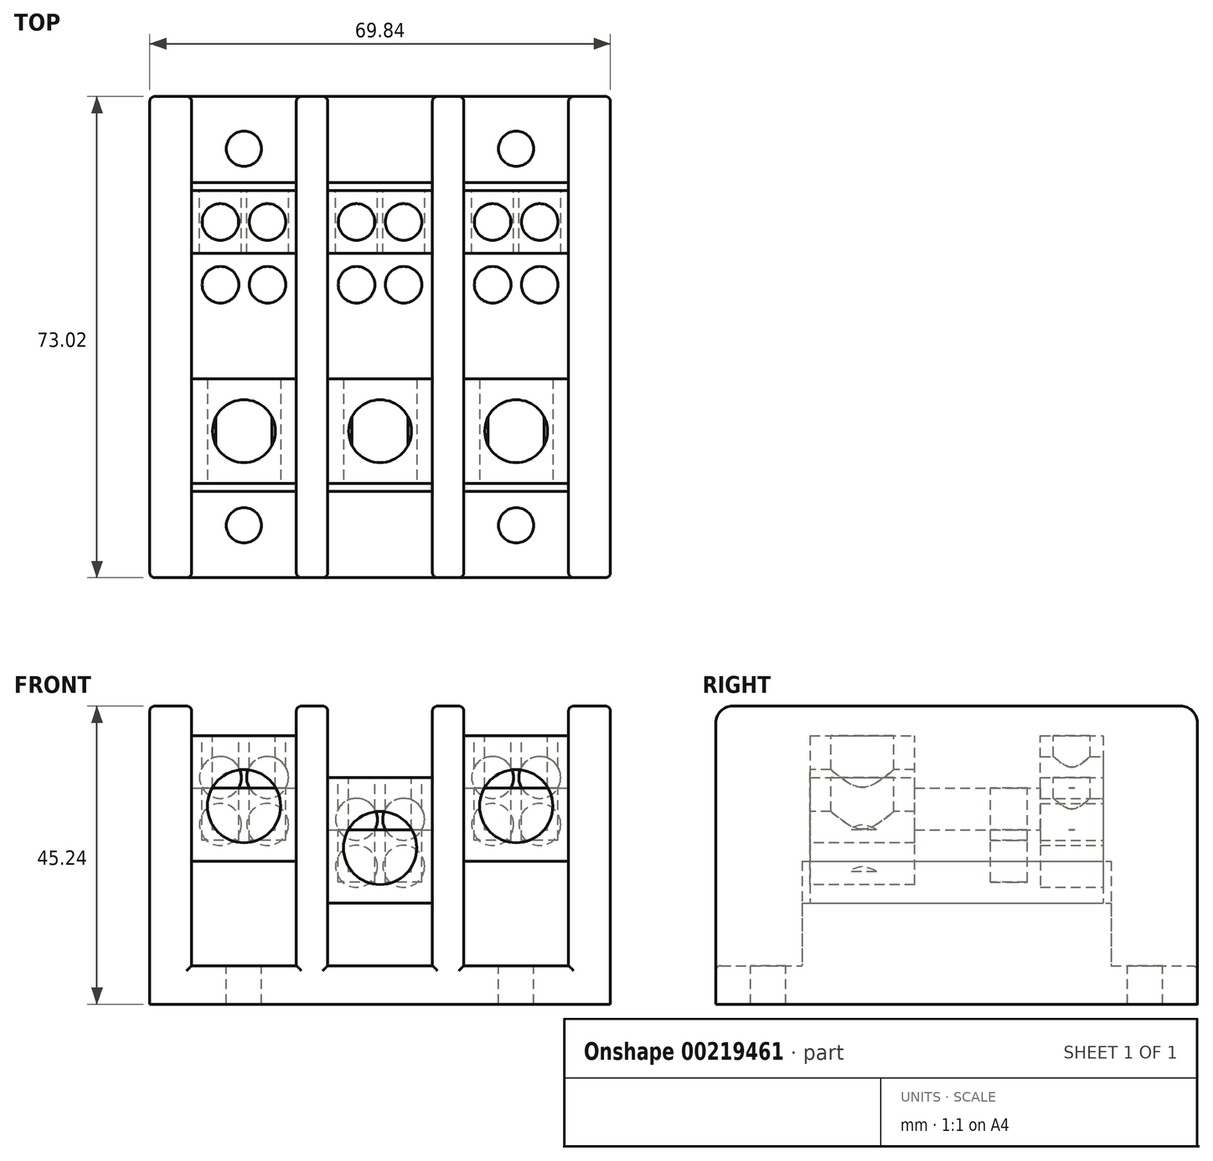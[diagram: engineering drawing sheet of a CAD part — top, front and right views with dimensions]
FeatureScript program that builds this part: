
annotation { "Feature Type Name" : "Feature", "Feature Type Description" : "" }
export const myFeature = defineFeature(function(context is Context, id is Id, definition is map)
    precondition{}
    {
        {
            var Q0;
            Q0=qCreatedBy(makeId("Top.planeOp"),FACE);
            var sketch = newSketch(context, id + "F0", { "sketchPlane" : qUnion([Q0])});
            skLineSegment(sketch, "E0.bottom", {"start": v(-34.92, -36.51) * mm, "end": v(34.93, -36.51) * mm});
            skLineSegment(sketch, "E0.top", {"start": v(-34.93, 36.51) * mm, "end": v(34.92, 36.51) * mm});
            skLineSegment(sketch, "E0.left", {"start": v(-34.92, -36.51) * mm, "end": v(-34.93, 36.51) * mm});
            skLineSegment(sketch, "E0.right", {"start": v(34.93, -36.51) * mm, "end": v(34.92, 36.51) * mm});
            skPoint(sketch, "E0.middle", {"position": v(0, 0) * mm});
            skSolve(sketch);
        }
        {
            var Q0;
            Q0=qSketchRegion(id+"F0",true);
            extrude(context, id + "F1", {"entities" : qUnion([Q0]), "depth" : 45.24 * mm});
        }
        {
            var Q0;
            Q0=makeQuery(id+"F1.opExtrude","CAP_FACE",FACE,{"disambiguationData":[OSD([sQuery(id+"F0.wireOp",EDGE,"E0.bottom"),sQuery(id+"F0.wireOp",EDGE,"E0.top"),sQuery(id+"F0.wireOp",EDGE,"E0.left"),sQuery(id+"F0.wireOp",EDGE,"E0.right")])],"isStart":false});
            var sketch = newSketch(context, id + "F2", { "sketchPlane" : qUnion([Q0])});
            skLineSegment(sketch, "E1.bottom", {"start": v(-12.7, -36.51) * mm, "end": v(-28.58, -36.51) * mm});
            skLineSegment(sketch, "E1.top", {"start": v(-12.7, 36.51) * mm, "end": v(-28.58, 36.51) * mm});
            skLineSegment(sketch, "E1.left", {"start": v(-12.7, -36.51) * mm, "end": v(-12.7, 36.51) * mm});
            skLineSegment(sketch, "E1.right", {"start": v(-28.58, -36.51) * mm, "end": v(-28.58, 36.51) * mm});
            skPoint(sketch, "E1.middle", {"position": v(-20.64, 0) * mm});
            skLineSegment(sketch, "E2.bottom", {"start": v(7.94, -36.51) * mm, "end": v(-7.94, -36.51) * mm});
            skLineSegment(sketch, "E2.top", {"start": v(7.94, 36.51) * mm, "end": v(-7.94, 36.51) * mm});
            skLineSegment(sketch, "E2.left", {"start": v(7.94, -36.51) * mm, "end": v(7.94, 36.51) * mm});
            skLineSegment(sketch, "E2.right", {"start": v(-7.94, -36.51) * mm, "end": v(-7.94, 36.51) * mm});
            skPoint(sketch, "E2.middle", {"position": v(0, 0) * mm});
            skLineSegment(sketch, "E3.bottom", {"start": v(28.58, -36.51) * mm, "end": v(12.7, -36.51) * mm});
            skLineSegment(sketch, "E3.top", {"start": v(28.58, 36.51) * mm, "end": v(12.7, 36.51) * mm});
            skLineSegment(sketch, "E3.left", {"start": v(28.58, -36.51) * mm, "end": v(28.58, 36.51) * mm});
            skLineSegment(sketch, "E3.right", {"start": v(12.7, -36.51) * mm, "end": v(12.7, 36.51) * mm});
            skPoint(sketch, "E3.middle", {"position": v(20.64, 0) * mm});
            skSolve(sketch);
        }
        {
            var Q0;
            Q0=qSketchRegion(id+"F2",true);
            extrude(context, id + "F3", {"entities" : qUnion([Q0]), "operationType" : NewBodyOperationType.REMOVE, "oppositeDirection" : true, "depth" : 39.4 * mm});
        }
        {
            var Q0;
            Q0=makeQuery(id+"F3.boolean.opBoolean","COPY",FACE,{"derivedFrom":makeQuery(id+"F3.opExtrude","CAP_FACE",FACE,{"disambiguationData":[OSD([sQuery(id+"F2.wireOp",EDGE,"E2.bottom"),sQuery(id+"F2.wireOp",EDGE,"E2.top"),sQuery(id+"F2.wireOp",EDGE,"E2.left"),sQuery(id+"F2.wireOp",EDGE,"E2.right")])],"isStart":false})});
            var sketch = newSketch(context, id + "F4", { "sketchPlane" : qUnion([Q0])});
            skCircle(sketch, "E4", {"center": v(-20.64, 28.57) * mm, "radius": 2.67 * mm});
            skCircle(sketch, "E5", {"center": v(-20.64, -28.58) * mm, "radius": 2.67 * mm});
            skCircle(sketch, "E6", {"center": v(20.64, 28.58) * mm, "radius": 2.67 * mm});
            skCircle(sketch, "E7", {"center": v(20.64, -28.57) * mm, "radius": 2.67 * mm});
            skSolve(sketch);
        }
        {
            var Q0;
            Q0=qSketchRegion(id+"F4",true);
            extrude(context, id + "F5", {"entities" : qUnion([Q0]), "operationType" : NewBodyOperationType.REMOVE, "oppositeDirection" : true, "depth" : 5.84 * mm});
        }
        {
            var Q0;
            {var subQ0=sQuery(id+"F0.wireOp",EDGE,"E0.left");var subQ1=sQuery(id+"F0.wireOp",EDGE,"E0.top");Q0=makeQuery(id+"F3.boolean.opBoolean","SPLIT",EDGE,{"disambiguationData":[TD([makeQuery(id+"F1.opExtrude","SWEPT_FACE",FACE,{"disambiguationData":[OSD([subQ0])]})])],"derivedFrom":makeQuery(id+"F1.opExtrude","CAP_EDGE",EDGE,{"disambiguationData":[OSD([subQ1])],"isStart":false})});}
            var Q1;
            {var subQ0=sQuery(id+"F0.wireOp",EDGE,"E0.top");Q1=makeQuery(id+"F3.boolean.opBoolean","SPLIT",EDGE,{"disambiguationData":[TD([makeQuery(id+"F3.opExtrude","SWEPT_FACE",FACE,{"disambiguationData":[OSD([sQuery(id+"F2.wireOp",EDGE,"E1.left")])]})])],"derivedFrom":makeQuery(id+"F1.opExtrude","CAP_EDGE",EDGE,{"disambiguationData":[OSD([subQ0])],"isStart":false})});}
            var Q2;
            {var subQ0=sQuery(id+"F0.wireOp",EDGE,"E0.top");Q2=makeQuery(id+"F3.boolean.opBoolean","SPLIT",EDGE,{"disambiguationData":[TD([makeQuery(id+"F3.opExtrude","SWEPT_FACE",FACE,{"disambiguationData":[OSD([sQuery(id+"F2.wireOp",EDGE,"E2.left")])]})])],"derivedFrom":makeQuery(id+"F1.opExtrude","CAP_EDGE",EDGE,{"disambiguationData":[OSD([subQ0])],"isStart":false})});}
            var Q3;
            {var subQ0=sQuery(id+"F0.wireOp",EDGE,"E0.right");var subQ1=sQuery(id+"F0.wireOp",EDGE,"E0.top");Q3=makeQuery(id+"F3.boolean.opBoolean","SPLIT",EDGE,{"disambiguationData":[TD([makeQuery(id+"F1.opExtrude","SWEPT_FACE",FACE,{"disambiguationData":[OSD([subQ0])]})])],"derivedFrom":makeQuery(id+"F1.opExtrude","CAP_EDGE",EDGE,{"disambiguationData":[OSD([subQ1])],"isStart":false})});}
            var Q4;
            {var subQ0=sQuery(id+"F0.wireOp",EDGE,"E0.bottom");var subQ1=sQuery(id+"F0.wireOp",EDGE,"E0.left");Q4=makeQuery(id+"F3.boolean.opBoolean","SPLIT",EDGE,{"disambiguationData":[TD([makeQuery(id+"F1.opExtrude","SWEPT_FACE",FACE,{"disambiguationData":[OSD([subQ1])]})])],"derivedFrom":makeQuery(id+"F1.opExtrude","CAP_EDGE",EDGE,{"disambiguationData":[OSD([subQ0])],"isStart":false})});}
            var Q5;
            {var subQ0=sQuery(id+"F0.wireOp",EDGE,"E0.bottom");Q5=makeQuery(id+"F3.boolean.opBoolean","SPLIT",EDGE,{"disambiguationData":[TD([makeQuery(id+"F3.opExtrude","SWEPT_FACE",FACE,{"disambiguationData":[OSD([sQuery(id+"F2.wireOp",EDGE,"E1.left")])]})])],"derivedFrom":makeQuery(id+"F1.opExtrude","CAP_EDGE",EDGE,{"disambiguationData":[OSD([subQ0])],"isStart":false})});}
            var Q6;
            {var subQ0=sQuery(id+"F0.wireOp",EDGE,"E0.bottom");Q6=makeQuery(id+"F3.boolean.opBoolean","SPLIT",EDGE,{"disambiguationData":[TD([makeQuery(id+"F3.opExtrude","SWEPT_FACE",FACE,{"disambiguationData":[OSD([sQuery(id+"F2.wireOp",EDGE,"E2.left")])]})])],"derivedFrom":makeQuery(id+"F1.opExtrude","CAP_EDGE",EDGE,{"disambiguationData":[OSD([subQ0])],"isStart":false})});}
            var Q7;
            {var subQ0=sQuery(id+"F0.wireOp",EDGE,"E0.bottom");var subQ1=sQuery(id+"F0.wireOp",EDGE,"E0.right");Q7=makeQuery(id+"F3.boolean.opBoolean","SPLIT",EDGE,{"disambiguationData":[TD([makeQuery(id+"F1.opExtrude","SWEPT_FACE",FACE,{"disambiguationData":[OSD([subQ1])]})])],"derivedFrom":makeQuery(id+"F1.opExtrude","CAP_EDGE",EDGE,{"disambiguationData":[OSD([subQ0])],"isStart":false})});}
            fillet(context, id + "F6", {"entities" : qUnion([Q0, Q1, Q2, Q3, Q4, Q5, Q6, Q7]), "radius" : 2.54 * mm, "tangentPropagation" : true});
        }
        {
            var Q0;
            Q0=makeQuery(id+"F1.opExtrude","SWEPT_EDGE",EDGE,{"disambiguationData":[OSD([sQuery(id+"F0.wireOp",EDGE,"E0.top"),sQuery(id+"F0.wireOp",EDGE,"E0.left")])]});
            var Q1;
            Q1=makeQuery(id+"F3.boolean.opBoolean","COPY",EDGE,{"derivedFrom":makeQuery(id+"F3.opExtrude","SWEPT_EDGE",EDGE,{"disambiguationData":[OSD([sQuery(id+"F0.wireOp",EDGE,"E0.top"),sQuery(id+"F2.wireOp",EDGE,"E1.top"),sQuery(id+"F2.wireOp",EDGE,"E1.right")])]})});
            var Q2;
            Q2=makeQuery(id+"F3.boolean.opBoolean","COPY",EDGE,{"derivedFrom":makeQuery(id+"F3.opExtrude","SWEPT_EDGE",EDGE,{"disambiguationData":[OSD([sQuery(id+"F0.wireOp",EDGE,"E0.top"),sQuery(id+"F2.wireOp",EDGE,"E1.top"),sQuery(id+"F2.wireOp",EDGE,"E1.left")])]})});
            var Q3;
            Q3=makeQuery(id+"F3.boolean.opBoolean","COPY",EDGE,{"derivedFrom":makeQuery(id+"F3.opExtrude","SWEPT_EDGE",EDGE,{"disambiguationData":[OSD([sQuery(id+"F0.wireOp",EDGE,"E0.top"),sQuery(id+"F2.wireOp",EDGE,"E2.top"),sQuery(id+"F2.wireOp",EDGE,"E2.right")])]})});
            var Q4;
            Q4=makeQuery(id+"F3.boolean.opBoolean","COPY",EDGE,{"derivedFrom":makeQuery(id+"F3.opExtrude","SWEPT_EDGE",EDGE,{"disambiguationData":[OSD([sQuery(id+"F0.wireOp",EDGE,"E0.top"),sQuery(id+"F2.wireOp",EDGE,"E2.top"),sQuery(id+"F2.wireOp",EDGE,"E2.left")])]})});
            var Q5;
            Q5=makeQuery(id+"F3.boolean.opBoolean","COPY",EDGE,{"derivedFrom":makeQuery(id+"F3.opExtrude","SWEPT_EDGE",EDGE,{"disambiguationData":[OSD([sQuery(id+"F0.wireOp",EDGE,"E0.top"),sQuery(id+"F2.wireOp",EDGE,"E3.top"),sQuery(id+"F2.wireOp",EDGE,"E3.right")])]})});
            var Q6;
            Q6=makeQuery(id+"F3.boolean.opBoolean","COPY",EDGE,{"derivedFrom":makeQuery(id+"F3.opExtrude","SWEPT_EDGE",EDGE,{"disambiguationData":[OSD([sQuery(id+"F0.wireOp",EDGE,"E0.top"),sQuery(id+"F2.wireOp",EDGE,"E3.top"),sQuery(id+"F2.wireOp",EDGE,"E3.left")])]})});
            var Q7;
            Q7=makeQuery(id+"F3.boolean.opBoolean","COPY",EDGE,{"derivedFrom":makeQuery(id+"F3.opExtrude","CAP_EDGE",EDGE,{"disambiguationData":[OSD([sQuery(id+"F2.wireOp",EDGE,"E3.top")])],"isStart":false})});
            var Q8;
            Q8=makeQuery(id+"F3.boolean.opBoolean","COPY",EDGE,{"derivedFrom":makeQuery(id+"F3.opExtrude","CAP_EDGE",EDGE,{"disambiguationData":[OSD([sQuery(id+"F2.wireOp",EDGE,"E2.top")])],"isStart":false})});
            var Q9;
            Q9=makeQuery(id+"F3.boolean.opBoolean","COPY",EDGE,{"derivedFrom":makeQuery(id+"F3.opExtrude","CAP_EDGE",EDGE,{"disambiguationData":[OSD([sQuery(id+"F2.wireOp",EDGE,"E1.top")])],"isStart":false})});
            var Q10;
            Q10=makeQuery(id+"F3.boolean.opBoolean","COPY",EDGE,{"derivedFrom":makeQuery(id+"F3.opExtrude","CAP_EDGE",EDGE,{"disambiguationData":[OSD([sQuery(id+"F2.wireOp",EDGE,"E1.bottom")])],"isStart":false})});
            var Q11;
            Q11=makeQuery(id+"F3.boolean.opBoolean","COPY",EDGE,{"derivedFrom":makeQuery(id+"F3.opExtrude","CAP_EDGE",EDGE,{"disambiguationData":[OSD([sQuery(id+"F2.wireOp",EDGE,"E2.bottom")])],"isStart":false})});
            var Q12;
            Q12=makeQuery(id+"F3.boolean.opBoolean","COPY",EDGE,{"derivedFrom":makeQuery(id+"F3.opExtrude","CAP_EDGE",EDGE,{"disambiguationData":[OSD([sQuery(id+"F2.wireOp",EDGE,"E3.bottom")])],"isStart":false})});
            var Q13;
            Q13=makeQuery(id+"F1.opExtrude","SWEPT_EDGE",EDGE,{"disambiguationData":[OSD([sQuery(id+"F0.wireOp",EDGE,"E0.bottom"),sQuery(id+"F0.wireOp",EDGE,"E0.right")])]});
            fillet(context, id + "F7", {"entities" : qUnion([Q0, Q1, Q2, Q3, Q4, Q5, Q6, Q7, Q8, Q9, Q10, Q11, Q12, Q13]), "radius" : 0.76 * mm, "tangentPropagation" : true});
        }
        {
            var Q0;
            Q0=makeQuery(id+"F3.boolean.opBoolean","COPY",FACE,{"derivedFrom":makeQuery(id+"F3.opExtrude","CAP_FACE",FACE,{"disambiguationData":[OSD([sQuery(id+"F2.wireOp",EDGE,"E1.bottom"),sQuery(id+"F2.wireOp",EDGE,"E1.top"),sQuery(id+"F2.wireOp",EDGE,"E1.left"),sQuery(id+"F2.wireOp",EDGE,"E1.right")])],"isStart":false})});
            var sketch = newSketch(context, id + "F8", { "sketchPlane" : qUnion([Q0])});
            skLineSegment(sketch, "E8.bottom", {"start": v(-28.58, 23.42) * mm, "end": v(-12.7, 23.42) * mm});
            skLineSegment(sketch, "E8.top", {"start": v(-28.58, -23.42) * mm, "end": v(-12.7, -23.42) * mm});
            skLineSegment(sketch, "E8.left", {"start": v(-28.58, 23.42) * mm, "end": v(-28.58, -23.42) * mm});
            skLineSegment(sketch, "E8.right", {"start": v(-12.7, 23.42) * mm, "end": v(-12.7, -23.42) * mm});
            skSolve(sketch);
        }
        {
            var Q0;
            Q0=qSketchRegion(id+"F8",true);
            extrude(context, id + "F9", {"entities" : qUnion([Q0]), "operationType" : NewBodyOperationType.ADD, "depth" : 15.88 * mm});
        }
        {
            var Q0;
            Q0=makeQuery(id+"F3.boolean.opBoolean","COPY",FACE,{"derivedFrom":makeQuery(id+"F3.opExtrude","CAP_FACE",FACE,{"disambiguationData":[OSD([sQuery(id+"F2.wireOp",EDGE,"E3.bottom"),sQuery(id+"F2.wireOp",EDGE,"E3.top"),sQuery(id+"F2.wireOp",EDGE,"E3.left"),sQuery(id+"F2.wireOp",EDGE,"E3.right")])],"isStart":false})});
            var sketch = newSketch(context, id + "F10", { "sketchPlane" : qUnion([Q0])});
            skLineSegment(sketch, "E9.bottom", {"start": v(12.7, 23.42) * mm, "end": v(28.58, 23.42) * mm});
            skLineSegment(sketch, "E9.top", {"start": v(12.7, -23.42) * mm, "end": v(28.58, -23.42) * mm});
            skLineSegment(sketch, "E9.left", {"start": v(12.7, 23.42) * mm, "end": v(12.7, -23.42) * mm});
            skLineSegment(sketch, "E9.right", {"start": v(28.58, 23.42) * mm, "end": v(28.58, -23.42) * mm});
            skSolve(sketch);
        }
        {
            var Q0;
            Q0=makeQuery(id+"F10.imprint","IMPRINT",FACE,{"disambiguationData":[TD([[makeQuery(id+"F10.imprint","IMPRINT",EDGE,{"derivedFrom":sQuery(id+"F10.wireOp",EDGE,"E9.bottom")}),-1.0]])]});
            extrude(context, id + "F11", {"entities" : qUnion([Q0]), "operationType" : NewBodyOperationType.ADD, "depth" : 15.88 * mm});
        }
        {
            var Q0;
            Q0=makeQuery(id+"F3.boolean.opBoolean","COPY",FACE,{"derivedFrom":makeQuery(id+"F3.opExtrude","CAP_FACE",FACE,{"disambiguationData":[OSD([sQuery(id+"F2.wireOp",EDGE,"E2.bottom"),sQuery(id+"F2.wireOp",EDGE,"E2.top"),sQuery(id+"F2.wireOp",EDGE,"E2.left"),sQuery(id+"F2.wireOp",EDGE,"E2.right")])],"isStart":false})});
            var sketch = newSketch(context, id + "F12", { "sketchPlane" : qUnion([Q0])});
            skLineSegment(sketch, "E10.bottom", {"start": v(-7.94, 23.42) * mm, "end": v(7.94, 23.42) * mm});
            skLineSegment(sketch, "E10.top", {"start": v(-7.94, -23.42) * mm, "end": v(7.94, -23.42) * mm});
            skLineSegment(sketch, "E10.left", {"start": v(-7.94, 23.42) * mm, "end": v(-7.94, -23.42) * mm});
            skLineSegment(sketch, "E10.right", {"start": v(7.94, 23.42) * mm, "end": v(7.94, -23.42) * mm});
            skSolve(sketch);
        }
        {
            var Q0;
            Q0=qSketchRegion(id+"F12",true);
            extrude(context, id + "F13", {"entities" : qUnion([Q0]), "operationType" : NewBodyOperationType.ADD, "depth" : 9.52 * mm});
        }
        {
            var Q0;
            Q0=makeQuery(id+"F9.opExtrude","CAP_FACE",FACE,{"disambiguationData":[OSD([sQuery(id+"F8.wireOp",EDGE,"E8.bottom"),sQuery(id+"F8.wireOp",EDGE,"E8.top"),sQuery(id+"F8.wireOp",EDGE,"E8.left"),sQuery(id+"F8.wireOp",EDGE,"E8.right")])],"isStart":false});
            var sketch = newSketch(context, id + "F14", { "sketchPlane" : qUnion([Q0])});
            skLineSegment(sketch, "E11.bottom", {"start": v(-28.57, -22.23) * mm, "end": v(-12.7, -22.23) * mm});
            skLineSegment(sketch, "E11.top", {"start": v(-28.58, 22.23) * mm, "end": v(-12.7, 22.23) * mm});
            skLineSegment(sketch, "E11.left", {"start": v(-28.57, -22.23) * mm, "end": v(-28.58, 22.23) * mm});
            skLineSegment(sketch, "E11.right", {"start": v(-12.7, -22.23) * mm, "end": v(-12.7, 22.23) * mm});
            skPoint(sketch, "E11.middle", {"position": v(-20.64, 0) * mm});
            skSolve(sketch);
        }
        {
            var Q0;
            Q0=qSketchRegion(id+"F14",true);
            extrude(context, id + "F15", {"entities" : qUnion([Q0]), "depth" : 19.05 * mm});
        }
        {
            var Q0;
            Q0=makeQuery(id+"F13.opExtrude","CAP_FACE",FACE,{"disambiguationData":[OSD([sQuery(id+"F12.wireOp",EDGE,"E10.bottom"),sQuery(id+"F12.wireOp",EDGE,"E10.top"),sQuery(id+"F12.wireOp",EDGE,"E10.left"),sQuery(id+"F12.wireOp",EDGE,"E10.right")])],"isStart":false});
            var sketch = newSketch(context, id + "F16", { "sketchPlane" : qUnion([Q0])});
            skLineSegment(sketch, "E12.bottom", {"start": v(-7.94, -22.22) * mm, "end": v(7.94, -22.22) * mm});
            skLineSegment(sketch, "E12.top", {"start": v(-7.94, 22.23) * mm, "end": v(7.94, 22.23) * mm});
            skLineSegment(sketch, "E12.left", {"start": v(-7.94, -22.22) * mm, "end": v(-7.94, 22.23) * mm});
            skLineSegment(sketch, "E12.right", {"start": v(7.94, -22.22) * mm, "end": v(7.94, 22.23) * mm});
            skPoint(sketch, "E12.middle", {"position": v(0, 0) * mm});
            skSolve(sketch);
        }
        {
            var Q0;
            Q0=makeQuery(id+"F16.imprint","IMPRINT",FACE,{"disambiguationData":[TD([[makeQuery(id+"F16.imprint","IMPRINT",EDGE,{"derivedFrom":sQuery(id+"F16.wireOp",EDGE,"E12.bottom")}),1.0]])]});
            extrude(context, id + "F17", {"entities" : qUnion([Q0]), "depth" : 19.05 * mm});
        }
        {
            var Q0;
            Q0=makeQuery(id+"F11.opExtrude","CAP_FACE",FACE,{"disambiguationData":[OSD([sQuery(id+"F10.wireOp",EDGE,"E9.bottom"),sQuery(id+"F10.wireOp",EDGE,"E9.top"),sQuery(id+"F10.wireOp",EDGE,"E9.left"),sQuery(id+"F10.wireOp",EDGE,"E9.right")])],"isStart":false});
            var sketch = newSketch(context, id + "F18", { "sketchPlane" : qUnion([Q0])});
            skLineSegment(sketch, "E13.bottom", {"start": v(12.7, -22.23) * mm, "end": v(28.58, -22.23) * mm});
            skLineSegment(sketch, "E13.top", {"start": v(12.7, 22.23) * mm, "end": v(28.58, 22.23) * mm});
            skLineSegment(sketch, "E13.left", {"start": v(12.7, -22.23) * mm, "end": v(12.7, 22.22) * mm});
            skLineSegment(sketch, "E13.right", {"start": v(28.58, -22.23) * mm, "end": v(28.58, 22.22) * mm});
            skPoint(sketch, "E13.middle", {"position": v(20.64, 0) * mm});
            skSolve(sketch);
        }
        {
            var Q0;
            Q0=qSketchRegion(id+"F18",true);
            extrude(context, id + "F19", {"entities" : qUnion([Q0]), "depth" : 19.05 * mm});
        }
        {
            var Q0;
            Q0=makeQuery(id+"F15.opExtrude","CAP_FACE",FACE,{"disambiguationData":[OSD([sQuery(id+"F14.wireOp",EDGE,"E11.bottom"),sQuery(id+"F14.wireOp",EDGE,"E11.top"),sQuery(id+"F14.wireOp",EDGE,"E11.left"),sQuery(id+"F14.wireOp",EDGE,"E11.right")])],"isStart":false});
            var sketch = newSketch(context, id + "F20", { "sketchPlane" : qUnion([Q0])});
            skLineSegment(sketch, "E14.bottom", {"start": v(-28.58, 12.7) * mm, "end": v(-12.7, 12.7) * mm});
            skLineSegment(sketch, "E14.top", {"start": v(-28.58, -6.35) * mm, "end": v(-12.7, -6.35) * mm});
            skLineSegment(sketch, "E14.left", {"start": v(-28.58, 12.7) * mm, "end": v(-28.58, -6.35) * mm});
            skLineSegment(sketch, "E14.right", {"start": v(-12.7, 12.7) * mm, "end": v(-12.7, -6.35) * mm});
            skSolve(sketch);
        }
        {
            var Q0;
            Q0=qSketchRegion(id+"F20",true);
            extrude(context, id + "F21", {"entities" : qUnion([Q0]), "operationType" : NewBodyOperationType.REMOVE, "oppositeDirection" : true, "depth" : 7.94 * mm});
        }
        {
            var Q0;
            {var subQ0=sQuery(id+"F14.wireOp",EDGE,"E11.top");var subQ1=sQuery(id+"F14.wireOp",EDGE,"E11.right");var subQ2=sQuery(id+"F14.wireOp",EDGE,"E11.left");Q0=makeQuery(id+"F21.boolean.opBoolean","SPLIT",FACE,{"disambiguationData":[TD([makeQuery(id+"F15.opExtrude","SWEPT_FACE",FACE,{"disambiguationData":[OSD([subQ0])]})])],"derivedFrom":makeQuery(id+"F15.opExtrude","CAP_FACE",FACE,{"disambiguationData":[OSD([sQuery(id+"F14.wireOp",EDGE,"E11.bottom"),subQ0,subQ2,subQ1])],"isStart":false})});}
            var sketch = newSketch(context, id + "F22", { "sketchPlane" : qUnion([Q0])});
            skCircle(sketch, "E15", {"center": v(-24.2, 17.46) * mm, "radius": 2.78 * mm});
            skCircle(sketch, "E16", {"center": v(-17.07, 17.46) * mm, "radius": 2.78 * mm});
            skPoint(sketch, "E17.centerSnap0", {"position": v(-20.64, -22.23) * mm});
            skSolve(sketch);
        }
        {
            var Q0;
            Q0=qSketchRegion(id+"F22",true);
            extrude(context, id + "F23", {"entities" : qUnion([Q0]), "operationType" : NewBodyOperationType.REMOVE, "oppositeDirection" : true, "depth" : 7.94 * mm});
        }
        {
            var Q0;
            {var subQ0=sQuery(id+"F14.wireOp",EDGE,"E11.bottom");var subQ1=sQuery(id+"F14.wireOp",EDGE,"E11.left");var subQ2=sQuery(id+"F14.wireOp",EDGE,"E11.right");Q0=makeQuery(id+"F21.boolean.opBoolean","SPLIT",FACE,{"disambiguationData":[TD([makeQuery(id+"F15.opExtrude","SWEPT_FACE",FACE,{"disambiguationData":[OSD([subQ0])]})])],"derivedFrom":makeQuery(id+"F15.opExtrude","CAP_FACE",FACE,{"disambiguationData":[OSD([subQ0,sQuery(id+"F14.wireOp",EDGE,"E11.top"),subQ1,subQ2])],"isStart":false})});}
            var sketch = newSketch(context, id + "F24", { "sketchPlane" : qUnion([Q0])});
            skCircle(sketch, "E18", {"center": v(-20.64, -14.29) * mm, "radius": 4.76 * mm});
            skPoint(sketch, "E18.centerSnap0", {"position": v(-28.58, -14.29) * mm});
            skPoint(sketch, "E18.centerSnap1", {"position": v(-20.64, -22.23) * mm});
            skSolve(sketch);
        }
        {
            var Q0;
            Q0=qSketchRegion(id+"F24",true);
            extrude(context, id + "F25", {"entities" : qUnion([Q0]), "operationType" : NewBodyOperationType.REMOVE, "oppositeDirection" : true, "depth" : 14.29 * mm});
        }
        {
            var Q0;
            Q0=makeQuery(id+"F21.boolean.opBoolean","COPY",FACE,{"derivedFrom":makeQuery(id+"F21.opExtrude","CAP_FACE",FACE,{"disambiguationData":[OSD([sQuery(id+"F20.wireOp",EDGE,"E14.bottom"),sQuery(id+"F20.wireOp",EDGE,"E14.top"),sQuery(id+"F20.wireOp",EDGE,"E14.left"),sQuery(id+"F20.wireOp",EDGE,"E14.right")])],"isStart":false})});
            var sketch = newSketch(context, id + "F26", { "sketchPlane" : qUnion([Q0])});
            skCircle(sketch, "E19", {"center": v(-24.2, 7.94) * mm, "radius": 2.78 * mm});
            skCircle(sketch, "E20", {"center": v(-17.07, 7.94) * mm, "radius": 2.78 * mm});
            skSolve(sketch);
        }
        {
            var Q0;
            Q0=qSketchRegion(id+"F26",true);
            extrude(context, id + "F27", {"entities" : qUnion([Q0]), "operationType" : NewBodyOperationType.REMOVE, "oppositeDirection" : true, "depth" : 7.94 * mm});
        }
        {
            var Q0;
            Q0=makeQuery(id+"F17.opExtrude","CAP_FACE",FACE,{"disambiguationData":[OSD([sQuery(id+"F16.wireOp",EDGE,"E12.bottom"),sQuery(id+"F16.wireOp",EDGE,"E12.top"),sQuery(id+"F16.wireOp",EDGE,"E12.left"),sQuery(id+"F16.wireOp",EDGE,"E12.right")])],"isStart":false});
            var sketch = newSketch(context, id + "F28", { "sketchPlane" : qUnion([Q0])});
            skLineSegment(sketch, "E21.bottom", {"start": v(-7.94, 12.7) * mm, "end": v(7.94, 12.7) * mm});
            skLineSegment(sketch, "E21.top", {"start": v(-7.94, -6.35) * mm, "end": v(7.94, -6.35) * mm});
            skLineSegment(sketch, "E21.left", {"start": v(-7.94, 12.7) * mm, "end": v(-7.94, -6.35) * mm});
            skLineSegment(sketch, "E21.right", {"start": v(7.94, 12.7) * mm, "end": v(7.94, -6.35) * mm});
            skSolve(sketch);
        }
        {
            var Q0;
            Q0=makeQuery(id+"F28.imprint","IMPRINT",FACE,{"disambiguationData":[TD([[makeQuery(id+"F28.imprint","IMPRINT",EDGE,{"derivedFrom":sQuery(id+"F28.wireOp",EDGE,"E21.bottom")}),-1.0]])]});
            extrude(context, id + "F29", {"entities" : qUnion([Q0]), "operationType" : NewBodyOperationType.REMOVE, "oppositeDirection" : true, "depth" : 7.94 * mm});
        }
        {
            var Q0;
            Q0=makeQuery(id+"F19.opExtrude","CAP_FACE",FACE,{"disambiguationData":[OSD([sQuery(id+"F18.wireOp",EDGE,"E13.bottom"),sQuery(id+"F18.wireOp",EDGE,"E13.top"),sQuery(id+"F18.wireOp",EDGE,"E13.left"),sQuery(id+"F18.wireOp",EDGE,"E13.right")])],"isStart":false});
            var sketch = newSketch(context, id + "F30", { "sketchPlane" : qUnion([Q0])});
            skLineSegment(sketch, "E22.bottom", {"start": v(12.7, 12.7) * mm, "end": v(28.58, 12.7) * mm});
            skLineSegment(sketch, "E22.top", {"start": v(12.7, -6.35) * mm, "end": v(28.58, -6.35) * mm});
            skLineSegment(sketch, "E22.left", {"start": v(12.7, 12.7) * mm, "end": v(12.7, -6.35) * mm});
            skLineSegment(sketch, "E22.right", {"start": v(28.58, 12.7) * mm, "end": v(28.58, -6.35) * mm});
            skSolve(sketch);
        }
        {
            var Q0;
            Q0=qSketchRegion(id+"F30",true);
            extrude(context, id + "F31", {"entities" : qUnion([Q0]), "operationType" : NewBodyOperationType.REMOVE, "oppositeDirection" : true, "depth" : 7.94 * mm});
        }
        {
            var Q0;
            {var subQ0=sQuery(id+"F16.wireOp",EDGE,"E12.top");var subQ1=sQuery(id+"F16.wireOp",EDGE,"E12.right");var subQ2=sQuery(id+"F16.wireOp",EDGE,"E12.left");Q0=makeQuery(id+"F29.boolean.opBoolean","SPLIT",FACE,{"disambiguationData":[TD([makeQuery(id+"F17.opExtrude","SWEPT_FACE",FACE,{"disambiguationData":[OSD([subQ0])]})])],"derivedFrom":makeQuery(id+"F17.opExtrude","CAP_FACE",FACE,{"disambiguationData":[OSD([sQuery(id+"F16.wireOp",EDGE,"E12.bottom"),subQ0,subQ2,subQ1])],"isStart":false})});}
            var sketch = newSketch(context, id + "F32", { "sketchPlane" : qUnion([Q0])});
            skCircle(sketch, "E23", {"center": v(-3.57, 17.46) * mm, "radius": 2.78 * mm});
            skPoint(sketch, "E23.centerSnap0", {"position": v(-7.94, 17.46) * mm});
            skCircle(sketch, "E24", {"center": v(3.57, 17.46) * mm, "radius": 2.78 * mm});
            skSolve(sketch);
        }
        {
            var Q0;
            Q0=qSketchRegion(id+"F32",true);
            extrude(context, id + "F33", {"entities" : qUnion([Q0]), "operationType" : NewBodyOperationType.REMOVE, "oppositeDirection" : true, "depth" : 7.94 * mm});
        }
        {
            var Q0;
            Q0=makeQuery(id+"F29.boolean.opBoolean","COPY",FACE,{"derivedFrom":makeQuery(id+"F29.opExtrude","CAP_FACE",FACE,{"disambiguationData":[OSD([sQuery(id+"F28.wireOp",EDGE,"E21.bottom"),sQuery(id+"F28.wireOp",EDGE,"E21.top"),sQuery(id+"F28.wireOp",EDGE,"E21.left"),sQuery(id+"F28.wireOp",EDGE,"E21.right")])],"isStart":false})});
            var sketch = newSketch(context, id + "F34", { "sketchPlane" : qUnion([Q0])});
            skCircle(sketch, "E25", {"center": v(-3.57, 7.94) * mm, "radius": 2.78 * mm});
            skCircle(sketch, "E26", {"center": v(3.57, 7.94) * mm, "radius": 2.78 * mm});
            skSolve(sketch);
        }
        {
            var Q0;
            Q0=qSketchRegion(id+"F34",true);
            extrude(context, id + "F35", {"entities" : qUnion([Q0]), "operationType" : NewBodyOperationType.REMOVE, "oppositeDirection" : true, "depth" : 7.94 * mm});
        }
        {
            var Q0;
            {var subQ0=sQuery(id+"F18.wireOp",EDGE,"E13.top");var subQ1=sQuery(id+"F18.wireOp",EDGE,"E13.right");var subQ2=sQuery(id+"F18.wireOp",EDGE,"E13.left");Q0=makeQuery(id+"F31.boolean.opBoolean","SPLIT",FACE,{"disambiguationData":[TD([makeQuery(id+"F19.opExtrude","SWEPT_FACE",FACE,{"disambiguationData":[OSD([subQ0])]})])],"derivedFrom":makeQuery(id+"F19.opExtrude","CAP_FACE",FACE,{"disambiguationData":[OSD([sQuery(id+"F18.wireOp",EDGE,"E13.bottom"),subQ0,subQ2,subQ1])],"isStart":false})});}
            var sketch = newSketch(context, id + "F36", { "sketchPlane" : qUnion([Q0])});
            skCircle(sketch, "E27", {"center": v(17.07, 17.46) * mm, "radius": 2.78 * mm});
            skPoint(sketch, "E27.centerSnap0", {"position": v(12.7, 17.46) * mm});
            skCircle(sketch, "E28", {"center": v(24.2, 17.46) * mm, "radius": 2.78 * mm});
            skPoint(sketch, "E28.centerSnap0", {"position": v(28.58, 17.46) * mm});
            skSolve(sketch);
        }
        {
            var Q0;
            Q0=qSketchRegion(id+"F36",true);
            extrude(context, id + "F37", {"entities" : qUnion([Q0]), "operationType" : NewBodyOperationType.REMOVE, "oppositeDirection" : true, "depth" : 7.94 * mm});
        }
        {
            var Q0;
            Q0=makeQuery(id+"F31.boolean.opBoolean","COPY",FACE,{"derivedFrom":makeQuery(id+"F31.opExtrude","CAP_FACE",FACE,{"disambiguationData":[OSD([sQuery(id+"F30.wireOp",EDGE,"E22.bottom"),sQuery(id+"F30.wireOp",EDGE,"E22.top"),sQuery(id+"F30.wireOp",EDGE,"E22.left"),sQuery(id+"F30.wireOp",EDGE,"E22.right")])],"isStart":false})});
            var sketch = newSketch(context, id + "F38", { "sketchPlane" : qUnion([Q0])});
            skCircle(sketch, "E29", {"center": v(17.07, 7.94) * mm, "radius": 2.78 * mm});
            skCircle(sketch, "E30", {"center": v(24.2, 7.94) * mm, "radius": 2.78 * mm});
            skSolve(sketch);
        }
        {
            var Q0;
            Q0=qSketchRegion(id+"F38",true);
            extrude(context, id + "F39", {"entities" : qUnion([Q0]), "operationType" : NewBodyOperationType.REMOVE, "oppositeDirection" : true, "depth" : 7.94 * mm});
        }
        {
            var Q0;
            {var subQ0=sQuery(id+"F16.wireOp",EDGE,"E12.bottom");var subQ1=sQuery(id+"F16.wireOp",EDGE,"E12.left");var subQ2=sQuery(id+"F16.wireOp",EDGE,"E12.right");Q0=makeQuery(id+"F29.boolean.opBoolean","SPLIT",FACE,{"disambiguationData":[TD([makeQuery(id+"F17.opExtrude","SWEPT_FACE",FACE,{"disambiguationData":[OSD([subQ0])]})])],"derivedFrom":makeQuery(id+"F17.opExtrude","CAP_FACE",FACE,{"disambiguationData":[OSD([subQ0,sQuery(id+"F16.wireOp",EDGE,"E12.top"),subQ1,subQ2])],"isStart":false})});}
            var sketch = newSketch(context, id + "F40", { "sketchPlane" : qUnion([Q0])});
            skCircle(sketch, "E31", {"center": v(0, -14.29) * mm, "radius": 4.76 * mm});
            skPoint(sketch, "E31.centerSnap0", {"position": v(-7.94, -14.29) * mm});
            skSolve(sketch);
        }
        {
            var Q0;
            Q0=makeQuery(id+"F40.imprint","IMPRINT",FACE,{"disambiguationData":[TD([[makeQuery(id+"F40.imprint","IMPRINT",EDGE,{"derivedFrom":sQuery(id+"F40.wireOp",EDGE,"E31")}),1.0]])]});
            extrude(context, id + "F41", {"entities" : qUnion([Q0]), "operationType" : NewBodyOperationType.REMOVE, "oppositeDirection" : true, "depth" : 14.29 * mm});
        }
        {
            var Q0;
            {var subQ0=sQuery(id+"F18.wireOp",EDGE,"E13.bottom");var subQ1=sQuery(id+"F18.wireOp",EDGE,"E13.left");var subQ2=sQuery(id+"F18.wireOp",EDGE,"E13.right");Q0=makeQuery(id+"F31.boolean.opBoolean","SPLIT",FACE,{"disambiguationData":[TD([makeQuery(id+"F19.opExtrude","SWEPT_FACE",FACE,{"disambiguationData":[OSD([subQ0])]})])],"derivedFrom":makeQuery(id+"F19.opExtrude","CAP_FACE",FACE,{"disambiguationData":[OSD([subQ0,sQuery(id+"F18.wireOp",EDGE,"E13.top"),subQ1,subQ2])],"isStart":false})});}
            var sketch = newSketch(context, id + "F42", { "sketchPlane" : qUnion([Q0])});
            skCircle(sketch, "E32", {"center": v(20.64, -14.29) * mm, "radius": 4.76 * mm});
            skPoint(sketch, "E32.centerSnap0", {"position": v(20.64, -6.35) * mm});
            skPoint(sketch, "E32.centerSnap1", {"position": v(12.7, -14.29) * mm});
            skSolve(sketch);
        }
        {
            var Q0;
            Q0=qSketchRegion(id+"F42",true);
            extrude(context, id + "F43", {"entities" : qUnion([Q0]), "operationType" : NewBodyOperationType.REMOVE, "oppositeDirection" : true, "depth" : 14.29 * mm});
        }
        {
            var Q0;
            Q0=makeQuery(id+"F15.opExtrude","SWEPT_FACE",FACE,{"disambiguationData":[OSD([sQuery(id+"F14.wireOp",EDGE,"E11.bottom")])]});
            var sketch = newSketch(context, id + "F44", { "sketchPlane" : qUnion([Q0])});
            skCircle(sketch, "E33", {"center": v(-20.64, 30.05) * mm, "radius": 5.56 * mm});
            skPoint(sketch, "E33.centerSnap0", {"position": v(-20.64, 21.72) * mm});
            skSolve(sketch);
        }
        {
            var Q0;
            Q0=qSketchRegion(id+"F44",true);
            extrude(context, id + "F45", {"entities" : qUnion([Q0]), "operationType" : NewBodyOperationType.REMOVE, "oppositeDirection" : true, "depth" : 15.88 * mm});
        }
        {
            var Q0;
            Q0=makeQuery(id+"F17.opExtrude","SWEPT_FACE",FACE,{"disambiguationData":[OSD([sQuery(id+"F16.wireOp",EDGE,"E12.bottom")])]});
            var sketch = newSketch(context, id + "F46", { "sketchPlane" : qUnion([Q0])});
            skCircle(sketch, "E34", {"center": v(0, 23.7) * mm, "radius": 5.56 * mm});
            skPoint(sketch, "E34.centerSnap0", {"position": v(0, 15.37) * mm});
            skSolve(sketch);
        }
        {
            var Q0;
            Q0=qSketchRegion(id+"F46",true);
            extrude(context, id + "F47", {"entities" : qUnion([Q0]), "operationType" : NewBodyOperationType.REMOVE, "oppositeDirection" : true, "depth" : 15.88 * mm});
        }
        {
            var Q0;
            Q0=makeQuery(id+"F19.opExtrude","SWEPT_FACE",FACE,{"disambiguationData":[OSD([sQuery(id+"F18.wireOp",EDGE,"E13.bottom")])]});
            var sketch = newSketch(context, id + "F48", { "sketchPlane" : qUnion([Q0])});
            skCircle(sketch, "E35", {"center": v(20.64, 30.05) * mm, "radius": 5.56 * mm});
            skPoint(sketch, "E35.centerSnap0", {"position": v(20.64, 21.72) * mm});
            skSolve(sketch);
        }
        {
            var Q0;
            Q0=qSketchRegion(id+"F48",true);
            extrude(context, id + "F49", {"entities" : qUnion([Q0]), "operationType" : NewBodyOperationType.REMOVE, "oppositeDirection" : true, "depth" : 15.88 * mm});
        }
        {
            var Q0;
            Q0=makeQuery(id+"F19.opExtrude","SWEPT_FACE",FACE,{"disambiguationData":[OSD([sQuery(id+"F18.wireOp",EDGE,"E13.top")])]});
            var sketch = newSketch(context, id + "F50", { "sketchPlane" : qUnion([Q0])});
            skCircle(sketch, "E36", {"center": v(-24.2, 34.42) * mm, "radius": 3.18 * mm});
            skCircle(sketch, "E37", {"center": v(-17.07, 34.42) * mm, "radius": 3.18 * mm});
            skCircle(sketch, "E38", {"center": v(-24.2, 27.27) * mm, "radius": 3.18 * mm});
            skCircle(sketch, "E39", {"center": v(-17.07, 27.27) * mm, "radius": 3.18 * mm});
            skSolve(sketch);
        }
        {
            var Q0;
            Q0=qSketchRegion(id+"F50",true);
            extrude(context, id + "F51", {"entities" : qUnion([Q0]), "operationType" : NewBodyOperationType.REMOVE, "oppositeDirection" : true, "depth" : 9.52 * mm});
        }
        {
            var Q0;
            Q0=makeQuery(id+"F17.opExtrude","SWEPT_FACE",FACE,{"disambiguationData":[OSD([sQuery(id+"F16.wireOp",EDGE,"E12.top")])]});
            var sketch = newSketch(context, id + "F52", { "sketchPlane" : qUnion([Q0])});
            skCircle(sketch, "E40", {"center": v(-3.57, 28.07) * mm, "radius": 3.18 * mm});
            skCircle(sketch, "E41", {"center": v(3.57, 28.07) * mm, "radius": 3.18 * mm});
            skCircle(sketch, "E42", {"center": v(-3.57, 20.92) * mm, "radius": 3.18 * mm});
            skCircle(sketch, "E43", {"center": v(3.57, 20.92) * mm, "radius": 3.18 * mm});
            skSolve(sketch);
        }
        {
            var Q0;
            Q0=qSketchRegion(id+"F52",true);
            extrude(context, id + "F53", {"entities" : qUnion([Q0]), "operationType" : NewBodyOperationType.REMOVE, "oppositeDirection" : true, "depth" : 9.52 * mm});
        }
        {
            var Q0;
            Q0=makeQuery(id+"F15.opExtrude","SWEPT_FACE",FACE,{"disambiguationData":[OSD([sQuery(id+"F14.wireOp",EDGE,"E11.top")])]});
            var sketch = newSketch(context, id + "F54", { "sketchPlane" : qUnion([Q0])});
            skCircle(sketch, "E44", {"center": v(17.07, 34.42) * mm, "radius": 3.18 * mm});
            skCircle(sketch, "E45", {"center": v(24.2, 34.42) * mm, "radius": 3.18 * mm});
            skCircle(sketch, "E46", {"center": v(17.07, 27.27) * mm, "radius": 3.18 * mm});
            skCircle(sketch, "E47", {"center": v(24.2, 27.27) * mm, "radius": 3.18 * mm});
            skSolve(sketch);
        }
        {
            var Q0;
            Q0=qSketchRegion(id+"F54",true);
            extrude(context, id + "F55", {"entities" : qUnion([Q0]), "operationType" : NewBodyOperationType.REMOVE, "oppositeDirection" : true, "depth" : 9.52 * mm});
        }
    });
